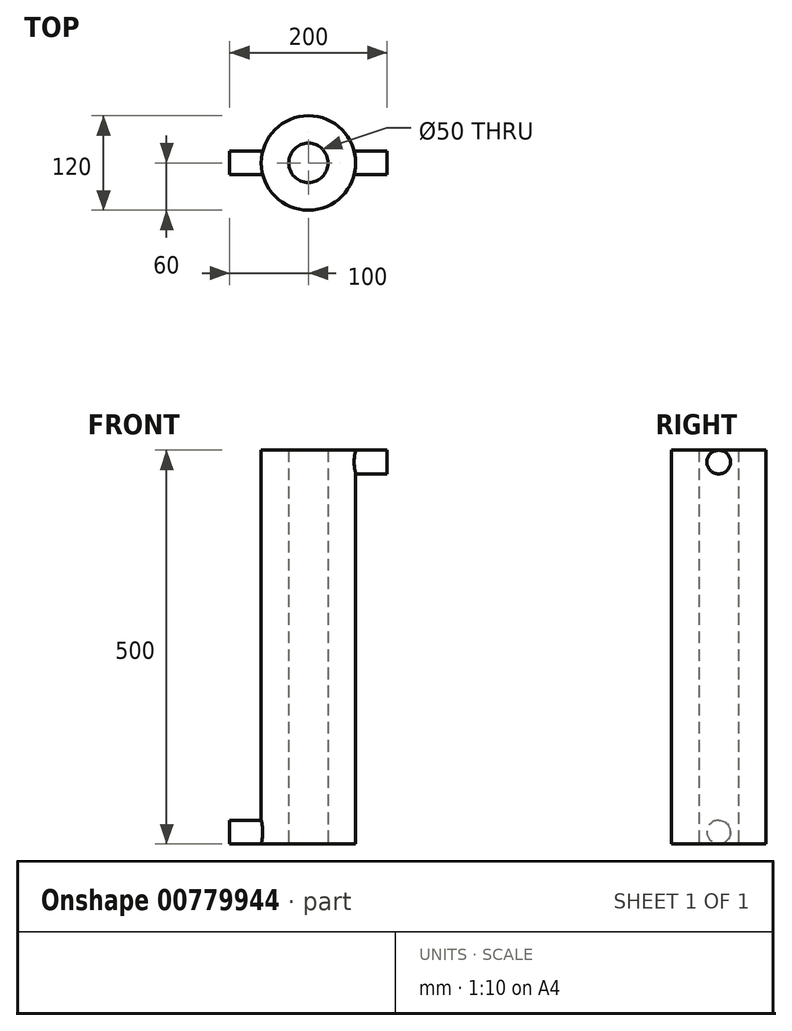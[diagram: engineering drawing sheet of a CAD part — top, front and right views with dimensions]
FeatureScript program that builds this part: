
annotation { "Feature Type Name" : "Feature", "Feature Type Description" : "" }
export const myFeature = defineFeature(function(context is Context, id is Id, definition is map)
    precondition{}
    {
        {
            var Q0;
            Q0=qCreatedBy(makeId("Top.planeOp"),FACE);
            var sketch = newSketch(context, id + "F0", { "sketchPlane" : qUnion([Q0])});
            skCircle(sketch, "E0", {"center": v(0, 0) * mm, "radius": 25 * mm});
            skCircle(sketch, "E1", {"center": v(0, 0) * mm, "radius": 60 * mm});
            skSolve(sketch);
        }
        {
            var Q0;
            Q0=qSketchRegion(id+"F0",true);
            extrude(context, id + "F1", {"entities" : qUnion([Q0]), "endBound" : BoundingType.SYMMETRIC, "depth" : 500 * mm, "offsetDistance" : 25.4 * mm});
        }
        {
            var Q0;
            Q0=qCreatedBy(makeId("Right.planeOp"),FACE);
            var sketch = newSketch(context, id + "F2", { "sketchPlane" : qUnion([Q0])});
            skCircle(sketch, "E2", {"center": v(0, 235) * mm, "radius": 15 * mm});
            skSolve(sketch);
        }
        {
            var Q0;
            Q0=qSketchRegion(id+"F2",true);
            var Q1;
            Q1=makeQuery(id+"F1.opExtrude","SWEPT_FACE",FACE,{"disambiguationData":[OSD([sQuery(id+"F0.wireOp",EDGE,"E1")])]});
            extrude(context, id + "F3", {"entities" : qUnion([Q0]), "operationType" : NewBodyOperationType.ADD, "depth" : 100 * mm, "offsetDistance" : 25 * mm, "hasSecondDirection" : true, "secondDirectionBound" : SecondDirectionBoundingType.UP_TO_SURFACE, "secondDirectionOppositeDirection" : false, "secondDirectionDepth" : 25 * mm, "secondDirectionBoundEntityFace" : qUnion([Q1]), "hasSecondDirectionOffset" : true, "secondDirectionOffsetDistance" : 0 * mm});
        }
        {
            var Q0;
            Q0=qCreatedBy(makeId("Right.planeOp"),FACE);
            var sketch = newSketch(context, id + "F4", { "sketchPlane" : qUnion([Q0])});
            skCircle(sketch, "E3", {"center": v(0, -235) * mm, "radius": 15 * mm});
            skSolve(sketch);
        }
        {
            var Q0;
            Q0=qSketchRegion(id+"F4",true);
            var Q1;
            Q1=makeQuery(id+"F1.opExtrude","SWEPT_FACE",FACE,{"disambiguationData":[OSD([sQuery(id+"F0.wireOp",EDGE,"E1")])]});
            extrude(context, id + "F5", {"entities" : qUnion([Q0]), "operationType" : NewBodyOperationType.ADD, "oppositeDirection" : true, "depth" : 100 * mm, "offsetDistance" : 25 * mm, "hasSecondDirection" : true, "secondDirectionBound" : SecondDirectionBoundingType.UP_TO_SURFACE, "secondDirectionOppositeDirection" : true, "secondDirectionDepth" : 25 * mm, "secondDirectionBoundEntityFace" : qUnion([Q1]), "hasSecondDirectionOffset" : true, "secondDirectionOffsetDistance" : 0 * mm});
        }
    });
